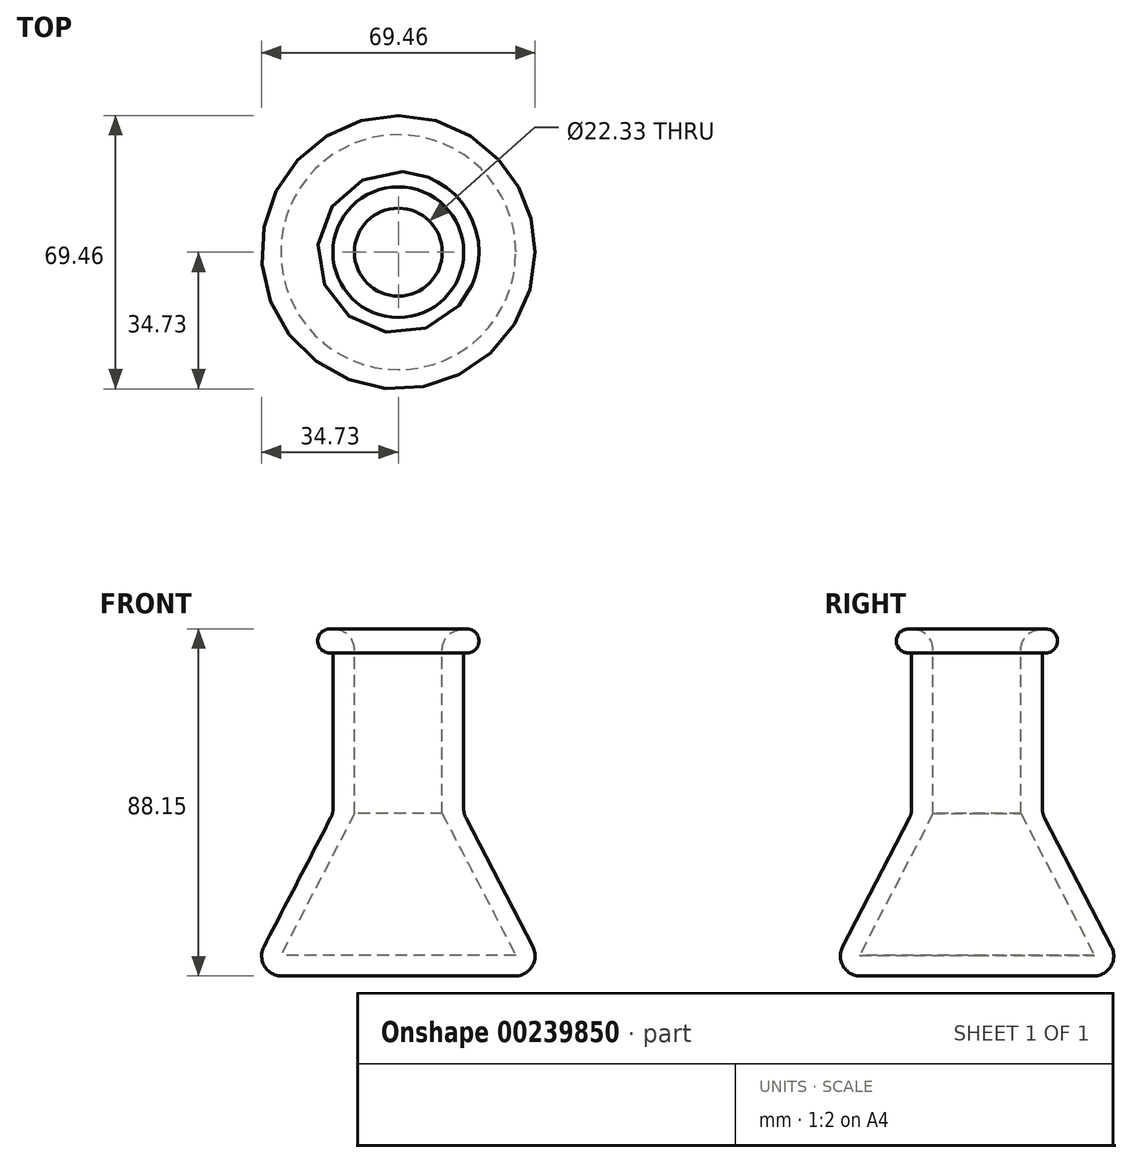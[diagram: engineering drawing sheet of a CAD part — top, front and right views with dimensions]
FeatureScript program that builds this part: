
annotation { "Feature Type Name" : "Feature", "Feature Type Description" : "" }
export const myFeature = defineFeature(function(context is Context, id is Id, definition is map)
    precondition{}
    {
        {
            var Q0;
            Q0=qCreatedBy(makeId("Front.planeOp"),FACE);
            var sketch = newSketch(context, id + "F0", { "sketchPlane" : qUnion([Q0])});
            skLineSegment(sketch, "E0", {"start": v(0, -41.24) * mm, "end": v(-38.01, -41.24) * mm});
            skLineSegment(sketch, "E1", {"start": v(-38.01, -41.24) * mm, "end": v(-16.6, 0) * mm});
            skLineSegment(sketch, "E2", {"start": v(-16.6, 0) * mm, "end": v(-16.6, 40.97) * mm});
            skArc(sketch, "E3", {"start": v(-16.6, 46.78) * mm, "mid": v(-20.5, 43.87) * mm, "end": v(-16.6, 40.97) * mm});
            skLineSegment(sketch, "E4", {"start": v(-16.6, 46.78) * mm, "end": v(-11.16, 46.78) * mm});
            skLineSegment(sketch, "E5", {"start": v(-11.16, 46.78) * mm, "end": v(-11.16, 0) * mm});
            skLineSegment(sketch, "E6", {"start": v(-11.16, 0) * mm, "end": v(-29.85, -36) * mm});
            skLineSegment(sketch, "E7", {"start": v(-29.85, -36) * mm, "end": v(0, -36) * mm});
            skLineSegment(sketch, "E8", {"start": v(0, -36) * mm, "end": v(0, -41.24) * mm});
            skSolve(sketch);
        }
        {
            var Q0;
            Q0 = qSketchRegion(id + "F0", true);
            var Q1;
            Q1=sQuery(id+"F0.wireOp",EDGE,"E8");
            revolve(context, id + "F1", {"entities" : qUnion([Q0]), "axis" : qUnion([Q1]), "revolveType" : RevolveType.FULL});
        }
        {
            var Q0;
            Q0=makeQuery(id+"F1.opRevolve","SWEPT_FACE",FACE,{"disambiguationData":[OSD([sQuery(id+"F0.wireOp",EDGE,"E1")])]});
            var Q1;
            Q1=makeQuery(id+"F1.opRevolve","SWEPT_EDGE",EDGE,{"disambiguationData":[OSD([sQuery(id+"F0.wireOp",EDGE,"E4"),sQuery(id+"F0.wireOp",EDGE,"E5")])]});
            fillet(context, id + "F2", {"entities" : qUnion([Q0, Q1]), "radius" : 5.08 * mm, "tangentPropagation" : true, "allowEdgeOverflow" : false});
        }
    });
